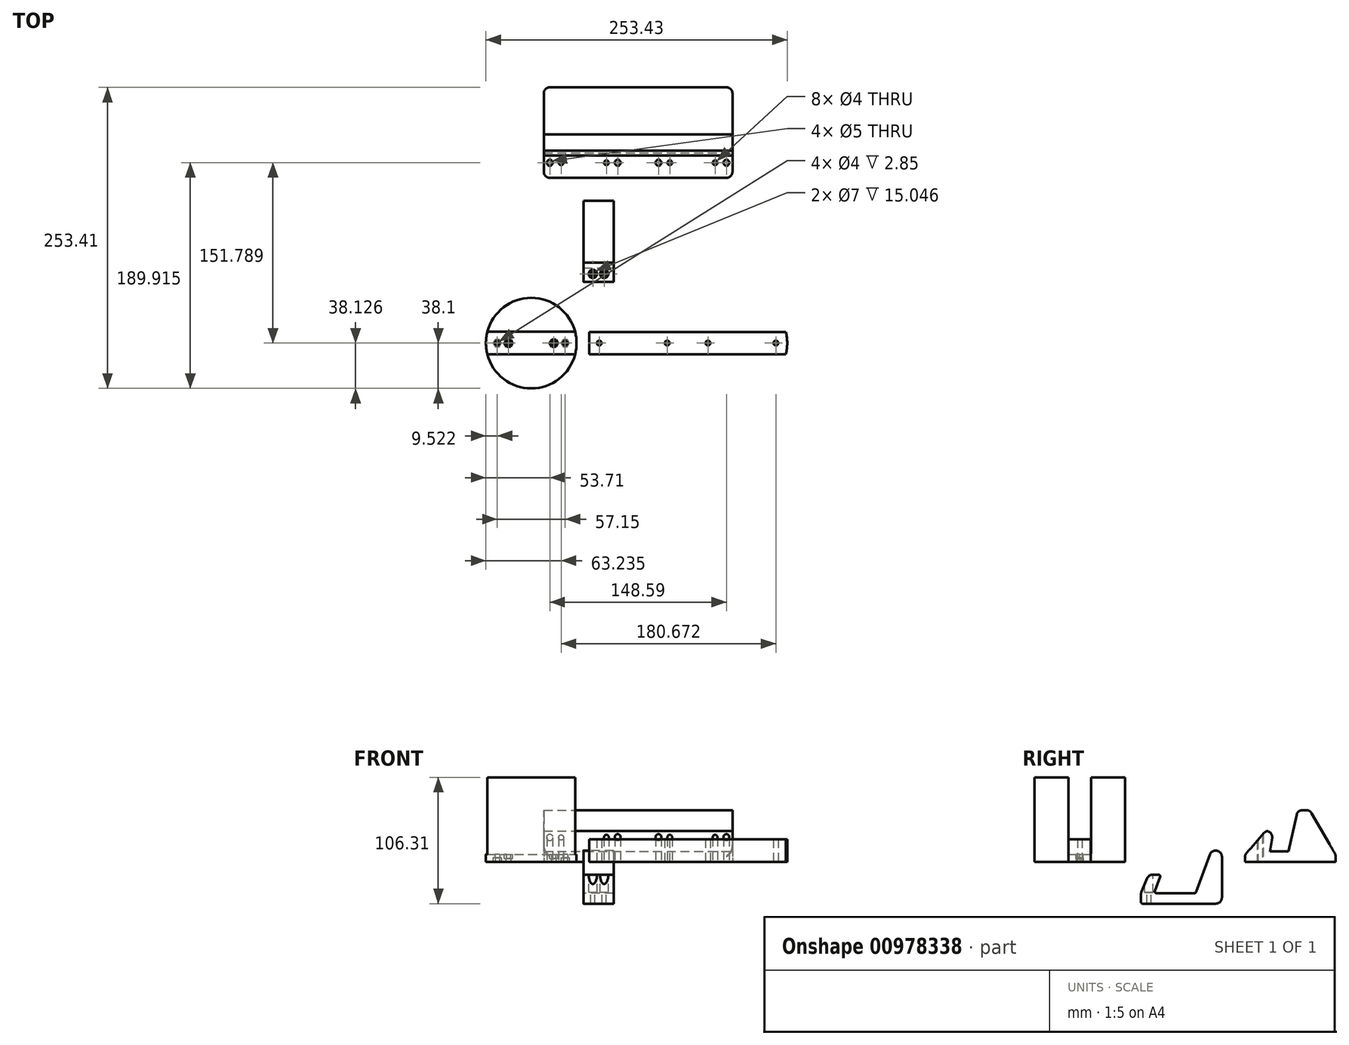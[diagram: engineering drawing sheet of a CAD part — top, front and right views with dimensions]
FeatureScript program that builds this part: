
annotation { "Feature Type Name" : "Feature", "Feature Type Description" : "" }
export const myFeature = defineFeature(function(context is Context, id is Id, definition is map)
    precondition{}
    {
        {
            var Q0;
            Q0=qCreatedBy(makeId("Top.planeOp"),FACE);
            var sketch = newSketch(context, id + "F0", { "sketchPlane" : qUnion([Q0])});
            skCircle(sketch, "E0", {"center": v(-43.87, -98.43) * mm, "radius": 38.1 * mm});
            skSolve(sketch);
        }
        {
            var Q0;
            Q0=makeQuery(id+"F0.imprint","IMPRINT",FACE,{"disambiguationData":[TD([[makeQuery(id+"F0.imprint","IMPRINT",EDGE,{"derivedFrom":sQuery(id+"F0.wireOp",EDGE,"E0")}),1.0]])]});
            extrude(context, id + "F1", {"entities" : qUnion([Q0]), "depth" : 71.12 * mm, "offsetDistance" : 25.4 * mm});
        }
        {
            var Q0;
            Q0=makeQuery(id+"F1.opExtrude","CAP_FACE",FACE,{"disambiguationData":[OSD([sQuery(id+"F0.wireOp",EDGE,"E0")])],"isStart":false});
            var sketch = newSketch(context, id + "F2", { "sketchPlane" : qUnion([Q0])});
            skCircle(sketch, "E1.0.0", {"center": v(-43.87, -98.43) * mm, "radius": 38.1 * mm, "construction": true});
            skLineSegment(sketch, "E2.bottom", {"start": v(-81.97, -88.9) * mm, "end": v(-5.77, -88.9) * mm});
            skLineSegment(sketch, "E2.top", {"start": v(-81.97, -107.96) * mm, "end": v(-5.77, -107.96) * mm});
            skLineSegment(sketch, "E2.left", {"start": v(-81.97, -88.9) * mm, "end": v(-81.97, -107.96) * mm});
            skLineSegment(sketch, "E2.right", {"start": v(-5.77, -88.9) * mm, "end": v(-5.77, -107.96) * mm});
            skSolve(sketch);
        }
        {
            var Q0;
            {var subQ0=sQuery(id+"F2.wireOp",EDGE,"E2.bottom");var subQ1=makeQuery(id+"F1.opExtrude","CAP_EDGE",EDGE,{"disambiguationData":[OSD([sQuery(id+"F0.wireOp",EDGE,"E0")])],"isStart":false});var subQ4=makeQuery(id+"F2.imprint","INTERSECT",VERTEX,{"disambiguationData":[OD(0.0)],"derivedFrom":[subQ1,subQ0]});Q0=makeQuery(id+"F2.imprint","IMPRINT",FACE,{"disambiguationData":[TD([[makeQuery(id+"F2.imprint","IMPRINT",EDGE,{"disambiguationData":[TD([[subQ4,-1.0]])],"derivedFrom":subQ0}),-1.0]])]});}
            extrude(context, id + "F3", {"entities" : qUnion([Q0]), "operationType" : NewBodyOperationType.REMOVE, "oppositeDirection" : true, "depth" : 64.77 * mm, "offsetDistance" : 25.4 * mm});
        }
        {
            var Q0;
            Q0=makeQuery(id+"F1.opExtrude","CAP_FACE",FACE,{"disambiguationData":[OSD([sQuery(id+"F0.wireOp",EDGE,"E0")])],"isStart":true});
            var sketch = newSketch(context, id + "F4", { "sketchPlane" : qUnion([Q0])});
            skArc(sketch, "E3.0.0", {"start": v(-80.76, 88.9) * mm, "mid": v(-81.97, 98.43) * mm, "end": v(-80.76, 107.96) * mm, "construction": true});
            skLineSegment(sketch, "E3.0.1", {"start": v(-80.76, 107.96) * mm, "end": v(-6.98, 107.96) * mm, "construction": true});
            skArc(sketch, "E3.0.2", {"start": v(-6.98, 107.96) * mm, "mid": v(-5.77, 98.43) * mm, "end": v(-6.98, 88.9) * mm, "construction": true});
            skLineSegment(sketch, "E3.0.3", {"start": v(-6.98, 88.9) * mm, "end": v(-80.76, 88.9) * mm, "construction": true});
            skLineSegment(sketch, "E4", {"start": v(-72.45, 98.43) * mm, "end": v(-15.3, 98.43) * mm, "construction": true});
            skCircle(sketch, "E5", {"center": v(-15.3, 98.43) * mm, "radius": 2 * mm});
            skCircle(sketch, "E6", {"center": v(-72.45, 98.43) * mm, "radius": 2 * mm});
            skCircle(sketch, "E7.cCircle", {"center": v(-72.45, 98.43) * mm, "radius": 3 * mm, "construction": true});
            skLineSegment(sketch, "E7.0", {"start": v(-74.18, 95.43) * mm, "end": v(-75.91, 98.43) * mm});
            skLineSegment(sketch, "E7.1", {"start": v(-75.91, 98.43) * mm, "end": v(-74.18, 101.43) * mm});
            skLineSegment(sketch, "E7.2", {"start": v(-74.18, 101.43) * mm, "end": v(-70.72, 101.43) * mm});
            skLineSegment(sketch, "E7.3", {"start": v(-70.72, 101.43) * mm, "end": v(-68.98, 98.43) * mm});
            skLineSegment(sketch, "E7.4", {"start": v(-68.98, 98.43) * mm, "end": v(-70.72, 95.43) * mm});
            skLineSegment(sketch, "E7.5", {"start": v(-70.72, 95.43) * mm, "end": v(-74.18, 95.43) * mm});
            skPoint(sketch, "E7.0.midPoint", {"position": v(-75.05, 96.93) * mm});
            skCircle(sketch, "E8.cCircle", {"center": v(-15.3, 98.43) * mm, "radius": 3 * mm, "construction": true});
            skLineSegment(sketch, "E8.0", {"start": v(-13.57, 95.43) * mm, "end": v(-17.03, 95.43) * mm});
            skLineSegment(sketch, "E8.1", {"start": v(-17.03, 95.43) * mm, "end": v(-18.76, 98.43) * mm});
            skLineSegment(sketch, "E8.2", {"start": v(-18.76, 98.43) * mm, "end": v(-17.03, 101.43) * mm});
            skLineSegment(sketch, "E8.3", {"start": v(-17.03, 101.43) * mm, "end": v(-13.57, 101.43) * mm});
            skLineSegment(sketch, "E8.4", {"start": v(-13.57, 101.43) * mm, "end": v(-11.83, 98.43) * mm});
            skLineSegment(sketch, "E8.5", {"start": v(-11.83, 98.43) * mm, "end": v(-13.57, 95.43) * mm});
            skPoint(sketch, "E8.0.midPoint", {"position": v(-15.3, 95.43) * mm});
            skSolve(sketch);
        }
        {
            var Q0;
            Q0=makeQuery(id+"F4.imprint","IMPRINT",FACE,{"disambiguationData":[TD([[makeQuery(id+"F4.imprint","IMPRINT",EDGE,{"derivedFrom":sQuery(id+"F4.wireOp",EDGE,"E6")}),-1.0]])]});
            var Q1;
            Q1=makeQuery(id+"F4.imprint","IMPRINT",FACE,{"disambiguationData":[TD([[makeQuery(id+"F4.imprint","IMPRINT",EDGE,{"derivedFrom":sQuery(id+"F4.wireOp",EDGE,"E5")}),-1.0]])]});
            extrude(context, id + "F5", {"entities" : qUnion([Q0, Q1]), "operationType" : NewBodyOperationType.REMOVE, "oppositeDirection" : true, "depth" : 3.5 * mm, "offsetDistance" : 25.4 * mm});
        }
        {
            var Q0;
            Q0=makeQuery(id+"F5.boolean.opBoolean","SPLIT",FACE,{"disambiguationData":[TD([makeQuery(id+"F5.opExtrude","SWEPT_FACE",FACE,{"disambiguationData":[OSD([sQuery(id+"F4.wireOp",EDGE,"E6")])]})])],"derivedFrom":makeQuery(id+"F1.opExtrude","CAP_FACE",FACE,{"disambiguationData":[OSD([sQuery(id+"F0.wireOp",EDGE,"E0")])],"isStart":true})});
            var Q1;
            Q1=makeQuery(id+"F4.imprint","IMPRINT",FACE,{"disambiguationData":[TD([[makeQuery(id+"F4.imprint","IMPRINT",EDGE,{"derivedFrom":sQuery(id+"F4.wireOp",EDGE,"E5")}),1.0]])]});
            extrude(context, id + "F6", {"entities" : qUnion([Q0, Q1]), "operationType" : NewBodyOperationType.REMOVE, "oppositeDirection" : true, "depth" : 25.4 * mm, "offsetDistance" : 25.4 * mm});
        }
        {
            var Q0;
            Q0=makeQuery(id+"F3.boolean.opBoolean","COPY",FACE,{"derivedFrom":makeQuery(id+"F3.opExtrude","CAP_FACE",FACE,{"disambiguationData":[OSD([sQuery(id+"F0.wireOp",EDGE,"E0"),sQuery(id+"F2.wireOp",EDGE,"E2.bottom"),sQuery(id+"F2.wireOp",EDGE,"E2.top")])],"isStart":false})});
            var sketch = newSketch(context, id + "F7", { "sketchPlane" : qUnion([Q0])});
            skArc(sketch, "E9.0.0", {"start": v(-80.76, -88.9) * mm, "mid": v(-81.97, -98.43) * mm, "end": v(-80.76, -107.96) * mm, "construction": true});
            skLineSegment(sketch, "E9.0.1", {"start": v(-80.76, -107.96) * mm, "end": v(-6.98, -107.96) * mm, "construction": true});
            skArc(sketch, "E9.0.2", {"start": v(-6.98, -107.96) * mm, "mid": v(-5.77, -98.43) * mm, "end": v(-6.98, -88.9) * mm, "construction": true});
            skLineSegment(sketch, "E9.0.3", {"start": v(-6.98, -88.9) * mm, "end": v(-80.76, -88.9) * mm, "construction": true});
            skCircle(sketch, "E10.0", {"center": v(-72.45, -98.43) * mm, "radius": 2 * mm, "construction": true});
            skCircle(sketch, "E11.0", {"center": v(-15.3, -98.43) * mm, "radius": 2 * mm, "construction": true});
            skLineSegment(sketch, "E12", {"start": v(-62.92, -98.43) * mm, "end": v(-24.82, -98.43) * mm, "construction": true});
            skCircle(sketch, "E13", {"center": v(-62.92, -98.43) * mm, "radius": 2 * mm});
            skCircle(sketch, "E14", {"center": v(-24.82, -98.43) * mm, "radius": 2 * mm});
            skCircle(sketch, "E15.cCircle", {"center": v(-62.92, -98.43) * mm, "radius": 3 * mm, "construction": true});
            skLineSegment(sketch, "E15.0", {"start": v(-61.2, -95.43) * mm, "end": v(-59.46, -98.43) * mm});
            skLineSegment(sketch, "E15.1", {"start": v(-59.46, -98.43) * mm, "end": v(-61.2, -101.43) * mm});
            skLineSegment(sketch, "E15.2", {"start": v(-61.2, -101.43) * mm, "end": v(-64.66, -101.43) * mm});
            skLineSegment(sketch, "E15.3", {"start": v(-64.66, -101.43) * mm, "end": v(-66.39, -98.43) * mm});
            skLineSegment(sketch, "E15.4", {"start": v(-66.39, -98.43) * mm, "end": v(-64.66, -95.43) * mm});
            skLineSegment(sketch, "E15.5", {"start": v(-64.66, -95.43) * mm, "end": v(-61.2, -95.43) * mm});
            skPoint(sketch, "E15.0.midPoint", {"position": v(-60.33, -96.93) * mm});
            skCircle(sketch, "E16.cCircle", {"center": v(-24.82, -98.43) * mm, "radius": 3 * mm, "construction": true});
            skLineSegment(sketch, "E16.0", {"start": v(-26.56, -95.43) * mm, "end": v(-23.1, -95.43) * mm});
            skLineSegment(sketch, "E16.1", {"start": v(-23.1, -95.43) * mm, "end": v(-21.36, -98.43) * mm});
            skLineSegment(sketch, "E16.2", {"start": v(-21.36, -98.43) * mm, "end": v(-23.1, -101.43) * mm});
            skLineSegment(sketch, "E16.3", {"start": v(-23.1, -101.43) * mm, "end": v(-26.56, -101.43) * mm});
            skLineSegment(sketch, "E16.4", {"start": v(-26.56, -101.43) * mm, "end": v(-28.29, -98.43) * mm});
            skLineSegment(sketch, "E16.5", {"start": v(-28.29, -98.43) * mm, "end": v(-26.56, -95.43) * mm});
            skPoint(sketch, "E16.0.midPoint", {"position": v(-24.82, -95.43) * mm});
            skSolve(sketch);
        }
        {
            var Q0;
            Q0=makeQuery(id+"F7.imprint","IMPRINT",FACE,{"disambiguationData":[TD([[makeQuery(id+"F7.imprint","IMPRINT",EDGE,{"derivedFrom":sQuery(id+"F7.wireOp",EDGE,"E13")}),-1.0]])]});
            var Q1;
            Q1=makeQuery(id+"F7.imprint","IMPRINT",FACE,{"disambiguationData":[TD([[makeQuery(id+"F7.imprint","IMPRINT",EDGE,{"derivedFrom":sQuery(id+"F7.wireOp",EDGE,"E14")}),-1.0]])]});
            extrude(context, id + "F8", {"entities" : qUnion([Q0, Q1]), "operationType" : NewBodyOperationType.REMOVE, "oppositeDirection" : true, "depth" : 3.5 * mm, "offsetDistance" : 25.4 * mm});
        }
        {
            var Q0;
            Q0=makeQuery(id+"F8.boolean.opBoolean","SPLIT",FACE,{"disambiguationData":[TD([makeQuery(id+"F8.opExtrude","SWEPT_FACE",FACE,{"disambiguationData":[OSD([sQuery(id+"F7.wireOp",EDGE,"E13")])]})])],"derivedFrom":makeQuery(id+"F3.boolean.opBoolean","COPY",FACE,{"derivedFrom":makeQuery(id+"F3.opExtrude","CAP_FACE",FACE,{"disambiguationData":[OSD([sQuery(id+"F0.wireOp",EDGE,"E0"),sQuery(id+"F2.wireOp",EDGE,"E2.bottom"),sQuery(id+"F2.wireOp",EDGE,"E2.top")])],"isStart":false})})});
            var Q1;
            Q1=makeQuery(id+"F8.boolean.opBoolean","SPLIT",FACE,{"disambiguationData":[TD([makeQuery(id+"F8.opExtrude","SWEPT_FACE",FACE,{"disambiguationData":[OSD([sQuery(id+"F7.wireOp",EDGE,"E14")])]})])],"derivedFrom":makeQuery(id+"F3.boolean.opBoolean","COPY",FACE,{"derivedFrom":makeQuery(id+"F3.opExtrude","CAP_FACE",FACE,{"disambiguationData":[OSD([sQuery(id+"F0.wireOp",EDGE,"E0"),sQuery(id+"F2.wireOp",EDGE,"E2.bottom"),sQuery(id+"F2.wireOp",EDGE,"E2.top")])],"isStart":false})})});
            extrude(context, id + "F9", {"entities" : qUnion([Q0, Q1]), "operationType" : NewBodyOperationType.REMOVE, "endBound" : BoundingType.THROUGH_ALL, "oppositeDirection" : true, "depth" : 25.4 * mm, "offsetDistance" : 25.4 * mm});
        }
        {
            var Q0;
            Q0=makeQuery(id+"F3.boolean.opBoolean","COPY",EDGE,{"derivedFrom":makeQuery(id+"F3.opExtrude","CAP_EDGE",EDGE,{"disambiguationData":[OSD([sQuery(id+"F2.wireOp",EDGE,"E2.top")])],"isStart":false})});
            var Q1;
            Q1=makeQuery(id+"F3.boolean.opBoolean","COPY",EDGE,{"derivedFrom":makeQuery(id+"F3.opExtrude","CAP_EDGE",EDGE,{"disambiguationData":[OSD([sQuery(id+"F2.wireOp",EDGE,"E2.bottom")])],"isStart":false})});
            fillet(context, id + "F10", {"entities" : qUnion([Q0, Q1]), "radius" : 0.5 * mm, "tangentPropagation" : true, "allowEdgeOverflow" : false});
        }
        {
            var Q0;
            Q0=qCreatedBy(makeId("Top.planeOp"),FACE);
            var sketch = newSketch(context, id + "F11", { "sketchPlane" : qUnion([Q0])});
            skLineSegment(sketch, "E17.bottom", {"start": v(5, -89) * mm, "end": v(170.28, -89) * mm});
            skLineSegment(sketch, "E17.top", {"start": v(5, -107.8) * mm, "end": v(170.28, -107.8) * mm});
            skLineSegment(sketch, "E17.left", {"start": v(5, -89) * mm, "end": v(5, -107.8) * mm});
            skLineSegment(sketch, "E17.right", {"start": v(170.28, -89) * mm, "end": v(170.28, -107.8) * mm, "construction": true});
            skPoint(sketch, "E17.middle", {"position": v(87.64, -98.4) * mm});
            skArc(sketch, "E18", {"start": v(5, -89) * mm, "mid": v(3.82, -98.4) * mm, "end": v(5, -107.8) * mm});
            skLineSegment(sketch, "E19", {"start": v(87.64, -89) * mm, "end": v(87.64, -107.8) * mm, "construction": true});
            skCircle(sketch, "E20", {"center": v(70.5, -98.4) * mm, "radius": 2 * mm});
            skCircle(sketch, "E21", {"center": v(13.35, -98.4) * mm, "radius": 2 * mm});
            skLineSegment(sketch, "E22", {"start": v(13.35, -98.4) * mm, "end": v(70.5, -98.4) * mm, "construction": true});
            skCircle(sketch, "E23.MirrorC", {"center": v(104.79, -98.4) * mm, "radius": 2 * mm});
            skCircle(sketch, "E24.MirrorC", {"center": v(161.94, -98.4) * mm, "radius": 2 * mm});
            skArc(sketch, "E25.MirrorCS", {"start": v(170.28, -89) * mm, "mid": v(171.46, -98.4) * mm, "end": v(170.28, -107.8) * mm});
            skCircle(sketch, "E26", {"center": v(41.92, -98.4) * mm, "radius": 38.1 * mm, "construction": true});
            skSolve(sketch);
        }
        {
            var Q0;
            Q0=makeQuery(id+"F11.imprint","IMPRINT",FACE,{"disambiguationData":[TD([[makeQuery(id+"F11.imprint","IMPRINT",EDGE,{"derivedFrom":sQuery(id+"F11.wireOp",EDGE,"E17.bottom")}),-1.0]])]});
            extrude(context, id + "F12", {"entities" : qUnion([Q0]), "depth" : 19.05 * mm, "offsetDistance" : 25.4 * mm});
        }
        {
            var Q0;
            Q0=qCreatedBy(makeId("Top.planeOp"),FACE);
            var sketch = newSketch(context, id + "F13", { "sketchPlane" : qUnion([Q0])});
            skCircle(sketch, "E27", {"center": v(-28.26, 53.38) * mm, "radius": 2.5 * mm});
            skCircle(sketch, "E28", {"center": v(-18.74, 53.38) * mm, "radius": 2 * mm});
            skCircle(sketch, "E29", {"center": v(19.36, 53.38) * mm, "radius": 2 * mm});
            skCircle(sketch, "E30", {"center": v(28.89, 53.38) * mm, "radius": 2.5 * mm});
            skLineSegment(sketch, "E31", {"start": v(-18.74, 53.38) * mm, "end": v(19.36, 53.38) * mm, "construction": true});
            skLineSegment(sketch, "E32", {"start": v(-28.26, 53.38) * mm, "end": v(-18.74, 53.38) * mm, "construction": true});
            skLineSegment(sketch, "E33", {"start": v(19.36, 53.38) * mm, "end": v(28.89, 53.38) * mm, "construction": true});
            skLineSegment(sketch, "E34", {"start": v(46.03, 60.68) * mm, "end": v(46.03, 43.66) * mm, "construction": true});
            skCircle(sketch, "E35.MirrorC", {"center": v(63.18, 53.38) * mm, "radius": 2.5 * mm});
            skCircle(sketch, "E36.MirrorC", {"center": v(72.7, 53.38) * mm, "radius": 2 * mm});
            skCircle(sketch, "E37.MirrorC", {"center": v(110.8, 53.38) * mm, "radius": 2 * mm});
            skCircle(sketch, "E38.MirrorC", {"center": v(120.33, 53.38) * mm, "radius": 2.5 * mm});
            skLineSegment(sketch, "E39.bottom", {"start": v(-33.34, 116.88) * mm, "end": v(125.4, 116.88) * mm});
            skLineSegment(sketch, "E39.top", {"start": v(-33.34, 40.68) * mm, "end": v(125.4, 40.68) * mm});
            skLineSegment(sketch, "E39.left", {"start": v(-33.34, 116.88) * mm, "end": v(-33.34, 40.68) * mm});
            skLineSegment(sketch, "E39.right", {"start": v(125.4, 116.88) * mm, "end": v(125.4, 40.68) * mm});
            skPoint(sketch, "E39.middle", {"position": v(46.03, 78.78) * mm});
            skSolve(sketch);
        }
        {
            var Q0;
            Q0=makeQuery(id+"F13.imprint","IMPRINT",FACE,{"disambiguationData":[TD([[makeQuery(id+"F13.imprint","IMPRINT",EDGE,{"derivedFrom":sQuery(id+"F13.wireOp",EDGE,"E27")}),-1.0]])]});
            extrude(context, id + "F14", {"entities" : qUnion([Q0]), "depth" : 6 * mm, "offsetDistance" : 25.4 * mm});
        }
        {
            var Q0;
            Q0=makeQuery(id+"F14.opExtrude","SWEPT_FACE",FACE,{"disambiguationData":[OSD([sQuery(id+"F13.wireOp",EDGE,"E39.right")])]});
            var sketch = newSketch(context, id + "F15", { "sketchPlane" : qUnion([Q0])});
            skLineSegment(sketch, "E40", {"start": v(40.68, 6) * mm, "end": v(58.17, 26) * mm});
            skLineSegment(sketch, "E41", {"start": v(58.17, 26) * mm, "end": v(64.4, 26) * mm});
            skLineSegment(sketch, "E42", {"start": v(64.4, 26) * mm, "end": v(61.72, 8.7) * mm});
            skLineSegment(sketch, "E43", {"start": v(61.72, 8.7) * mm, "end": v(77.3, 8.7) * mm});
            skLineSegment(sketch, "E44", {"start": v(77.3, 8.7) * mm, "end": v(84.94, 43.52) * mm});
            skLineSegment(sketch, "E45", {"start": v(84.94, 43.52) * mm, "end": v(95.26, 43.52) * mm});
            skLineSegment(sketch, "E46", {"start": v(95.26, 43.52) * mm, "end": v(116.88, 6) * mm});
            skSolve(sketch);
        }
        {
            var Q0;
            Q0=makeQuery(id+"F15.imprint","IMPRINT",FACE,{"disambiguationData":[TD([[makeQuery(id+"F15.imprint","IMPRINT",EDGE,{"derivedFrom":sQuery(id+"F15.wireOp",EDGE,"E40")}),-1.0]])]});
            var Q1;
            Q1=makeQuery(id+"F14.opExtrude","SWEPT_FACE",FACE,{"disambiguationData":[OSD([sQuery(id+"F13.wireOp",EDGE,"E39.left")])]});
            extrude(context, id + "F16", {"entities" : qUnion([Q0]), "operationType" : NewBodyOperationType.ADD, "endBound" : BoundingType.UP_TO_SURFACE, "oppositeDirection" : true, "depth" : 25.4 * mm, "endBoundEntityFace" : qUnion([Q1]), "offsetDistance" : 25.4 * mm});
        }
        {
            var Q0;
            {var subQ0=sQuery(id+"F13.wireOp",EDGE,"E39.top");Q0=makeQuery(id+"F16.boolean.opBoolean","MERGE",EDGE,{"derivedFrom":[makeQuery(id+"F14.opExtrude","CAP_EDGE",EDGE,{"disambiguationData":[OSD([subQ0])],"isStart":false}),makeQuery(id+"F16.opExtrude","SWEPT_EDGE",EDGE,{"disambiguationData":[OSD([subQ0,sQuery(id+"F13.wireOp",EDGE,"E39.right"),sQuery(id+"F15.wireOp",EDGE,"E40")])]})]});}
            var Q1;
            Q1=makeQuery(id+"F16.opExtrude","SWEPT_EDGE",EDGE,{"disambiguationData":[OSD([sQuery(id+"F15.wireOp",EDGE,"E40"),sQuery(id+"F15.wireOp",EDGE,"E41")])]});
            var Q2;
            Q2=makeQuery(id+"F14.opExtrude","SWEPT_EDGE",EDGE,{"disambiguationData":[OSD([sQuery(id+"F13.wireOp",EDGE,"E39.top"),sQuery(id+"F13.wireOp",EDGE,"E39.left")])]});
            var Q3;
            Q3=makeQuery(id+"F14.opExtrude","SWEPT_EDGE",EDGE,{"disambiguationData":[OSD([sQuery(id+"F13.wireOp",EDGE,"E39.top"),sQuery(id+"F13.wireOp",EDGE,"E39.right")])]});
            var Q4;
            {var subQ0=sQuery(id+"F13.wireOp",EDGE,"E39.bottom");Q4=makeQuery(id+"F16.boolean.opBoolean","MERGE",EDGE,{"derivedFrom":[makeQuery(id+"F14.opExtrude","CAP_EDGE",EDGE,{"disambiguationData":[OSD([subQ0])],"isStart":false}),makeQuery(id+"F16.opExtrude","SWEPT_EDGE",EDGE,{"disambiguationData":[OSD([subQ0,sQuery(id+"F13.wireOp",EDGE,"E39.right"),sQuery(id+"F15.wireOp",EDGE,"E46")])]})]});}
            var Q5;
            Q5=makeQuery(id+"F14.opExtrude","SWEPT_EDGE",EDGE,{"disambiguationData":[OSD([sQuery(id+"F13.wireOp",EDGE,"E39.bottom"),sQuery(id+"F13.wireOp",EDGE,"E39.right")])]});
            var Q6;
            Q6=makeQuery(id+"F14.opExtrude","SWEPT_EDGE",EDGE,{"disambiguationData":[OSD([sQuery(id+"F13.wireOp",EDGE,"E39.bottom"),sQuery(id+"F13.wireOp",EDGE,"E39.left")])]});
            var Q7;
            Q7=makeQuery(id+"F16.opExtrude","SWEPT_EDGE",EDGE,{"disambiguationData":[OSD([sQuery(id+"F15.wireOp",EDGE,"E45"),sQuery(id+"F15.wireOp",EDGE,"E46")])]});
            var Q8;
            Q8=makeQuery(id+"F16.opExtrude","SWEPT_EDGE",EDGE,{"disambiguationData":[OSD([sQuery(id+"F15.wireOp",EDGE,"E44"),sQuery(id+"F15.wireOp",EDGE,"E45")])]});
            var Q9;
            Q9=makeQuery(id+"F16.opExtrude","SWEPT_EDGE",EDGE,{"disambiguationData":[OSD([sQuery(id+"F15.wireOp",EDGE,"E41"),sQuery(id+"F15.wireOp",EDGE,"E42")])]});
            fillet(context, id + "F17", {"entities" : qUnion([Q0, Q1, Q2, Q3, Q4, Q5, Q6, Q7, Q8, Q9]), "radius" : 5.08 * mm, "tangentPropagation" : true, "allowEdgeOverflow" : false});
        }
        {
            var Q0;
            Q0=makeQuery(id+"F16.boolean.opBoolean","SPLIT",FACE,{"disambiguationData":[TD([makeQuery(id+"F14.opExtrude","SWEPT_FACE",FACE,{"disambiguationData":[OSD([sQuery(id+"F13.wireOp",EDGE,"E27")])]})])],"derivedFrom":makeQuery(id+"F16.opExtrude","SWEPT_FACE",FACE,{"disambiguationData":[OSD([sQuery(id+"F13.wireOp",EDGE,"E39.right")])]})});
            var Q1;
            Q1=makeQuery(id+"F16.boolean.opBoolean","SPLIT",FACE,{"disambiguationData":[TD([makeQuery(id+"F14.opExtrude","SWEPT_FACE",FACE,{"disambiguationData":[OSD([sQuery(id+"F13.wireOp",EDGE,"E28")])]})])],"derivedFrom":makeQuery(id+"F16.opExtrude","SWEPT_FACE",FACE,{"disambiguationData":[OSD([sQuery(id+"F13.wireOp",EDGE,"E39.right")])]})});
            var Q2;
            Q2=makeQuery(id+"F16.boolean.opBoolean","SPLIT",FACE,{"disambiguationData":[TD([makeQuery(id+"F14.opExtrude","SWEPT_FACE",FACE,{"disambiguationData":[OSD([sQuery(id+"F13.wireOp",EDGE,"E35.MirrorC")])]})])],"derivedFrom":makeQuery(id+"F16.opExtrude","SWEPT_FACE",FACE,{"disambiguationData":[OSD([sQuery(id+"F13.wireOp",EDGE,"E39.right")])]})});
            var Q3;
            Q3=makeQuery(id+"F16.boolean.opBoolean","SPLIT",FACE,{"disambiguationData":[TD([makeQuery(id+"F14.opExtrude","SWEPT_FACE",FACE,{"disambiguationData":[OSD([sQuery(id+"F13.wireOp",EDGE,"E30")])]})])],"derivedFrom":makeQuery(id+"F16.opExtrude","SWEPT_FACE",FACE,{"disambiguationData":[OSD([sQuery(id+"F13.wireOp",EDGE,"E39.right")])]})});
            var Q4;
            Q4=makeQuery(id+"F16.boolean.opBoolean","SPLIT",FACE,{"disambiguationData":[TD([makeQuery(id+"F14.opExtrude","SWEPT_FACE",FACE,{"disambiguationData":[OSD([sQuery(id+"F13.wireOp",EDGE,"E38.MirrorC")])]})])],"derivedFrom":makeQuery(id+"F16.opExtrude","SWEPT_FACE",FACE,{"disambiguationData":[OSD([sQuery(id+"F13.wireOp",EDGE,"E39.right")])]})});
            var Q5;
            Q5=makeQuery(id+"F16.boolean.opBoolean","SPLIT",FACE,{"disambiguationData":[TD([makeQuery(id+"F14.opExtrude","SWEPT_FACE",FACE,{"disambiguationData":[OSD([sQuery(id+"F13.wireOp",EDGE,"E37.MirrorC")])]})])],"derivedFrom":makeQuery(id+"F16.opExtrude","SWEPT_FACE",FACE,{"disambiguationData":[OSD([sQuery(id+"F13.wireOp",EDGE,"E39.right")])]})});
            var Q6;
            Q6=makeQuery(id+"F16.boolean.opBoolean","SPLIT",FACE,{"disambiguationData":[TD([makeQuery(id+"F14.opExtrude","SWEPT_FACE",FACE,{"disambiguationData":[OSD([sQuery(id+"F13.wireOp",EDGE,"E29")])]})])],"derivedFrom":makeQuery(id+"F16.opExtrude","SWEPT_FACE",FACE,{"disambiguationData":[OSD([sQuery(id+"F13.wireOp",EDGE,"E39.right")])]})});
            var Q7;
            Q7=makeQuery(id+"F16.boolean.opBoolean","SPLIT",FACE,{"disambiguationData":[TD([makeQuery(id+"F14.opExtrude","SWEPT_FACE",FACE,{"disambiguationData":[OSD([sQuery(id+"F13.wireOp",EDGE,"E36.MirrorC")])]})])],"derivedFrom":makeQuery(id+"F16.opExtrude","SWEPT_FACE",FACE,{"disambiguationData":[OSD([sQuery(id+"F13.wireOp",EDGE,"E39.right")])]})});
            extrude(context, id + "F18", {"entities" : qUnion([Q0, Q1, Q2, Q3, Q4, Q5, Q6, Q7]), "operationType" : NewBodyOperationType.REMOVE, "endBound" : BoundingType.THROUGH_ALL, "oppositeDirection" : true, "depth" : 25.4 * mm, "offsetDistance" : 25.4 * mm});
        }
        {
            var Q0;
            Q0=qCreatedBy(makeId("Right.planeOp"),FACE);
            var sketch = newSketch(context, id + "F19", { "sketchPlane" : qUnion([Q0])});
            skLineSegment(sketch, "E47", {"start": v(-46.85, -26.3) * mm, "end": v(-40.37, -10.78) * mm});
            skLineSegment(sketch, "E48", {"start": v(-40.37, -10.78) * mm, "end": v(-30.2, -10.78) * mm});
            skLineSegment(sketch, "E49", {"start": v(-30.2, -10.78) * mm, "end": v(-35.85, -26.3) * mm});
            skLineSegment(sketch, "E50", {"start": v(-35.85, -26.3) * mm, "end": v(-0.72, -26.3) * mm});
            skLineSegment(sketch, "E51", {"start": v(-0.72, -26.3) * mm, "end": v(12.32, 9.5) * mm});
            skLineSegment(sketch, "E52", {"start": v(12.32, 9.5) * mm, "end": v(21.2, 9.5) * mm});
            skLineSegment(sketch, "E53", {"start": v(21.2, 9.5) * mm, "end": v(21.2, -26.3) * mm});
            skLineSegment(sketch, "E54", {"start": v(21.2, -26.3) * mm, "end": v(21.2, -35.19) * mm});
            skLineSegment(sketch, "E55", {"start": v(21.2, -35.19) * mm, "end": v(-46.85, -35.19) * mm});
            skLineSegment(sketch, "E56", {"start": v(-46.85, -35.19) * mm, "end": v(-46.85, -26.3) * mm});
            skSolve(sketch);
        }
        {
            var Q0;
            Q0=makeQuery(id+"F19.imprint","IMPRINT",FACE,{"disambiguationData":[TD([[makeQuery(id+"F19.imprint","IMPRINT",EDGE,{"derivedFrom":sQuery(id+"F19.wireOp",EDGE,"E47")}),-1.0]])]});
            extrude(context, id + "F20", {"entities" : qUnion([Q0]), "depth" : 25.4 * mm, "offsetDistance" : 25.4 * mm});
        }
        {
            var Q0;
            Q0=makeQuery(id+"F20.opExtrude","SWEPT_EDGE",EDGE,{"disambiguationData":[OSD([sQuery(id+"F19.wireOp",EDGE,"E51"),sQuery(id+"F19.wireOp",EDGE,"E52")])]});
            var Q1;
            Q1=makeQuery(id+"F20.opExtrude","SWEPT_EDGE",EDGE,{"disambiguationData":[OSD([sQuery(id+"F19.wireOp",EDGE,"E52"),sQuery(id+"F19.wireOp",EDGE,"E53")])]});
            var Q2;
            Q2=makeQuery(id+"F20.opExtrude","SWEPT_EDGE",EDGE,{"disambiguationData":[OSD([sQuery(id+"F19.wireOp",EDGE,"E54"),sQuery(id+"F19.wireOp",EDGE,"E55")])]});
            var Q3;
            Q3=makeQuery(id+"F20.opExtrude","SWEPT_EDGE",EDGE,{"disambiguationData":[OSD([sQuery(id+"F19.wireOp",EDGE,"E47"),sQuery(id+"F19.wireOp",EDGE,"E56")])]});
            var Q4;
            Q4=makeQuery(id+"F20.opExtrude","SWEPT_EDGE",EDGE,{"disambiguationData":[OSD([sQuery(id+"F19.wireOp",EDGE,"E47"),sQuery(id+"F19.wireOp",EDGE,"E48")])]});
            fillet(context, id + "F21", {"entities" : qUnion([Q0, Q1, Q2, Q3, Q4]), "radius" : 5.08 * mm, "tangentPropagation" : true, "allowEdgeOverflow" : false});
        }
        {
            var Q0;
            Q0=makeQuery(id+"F20.opExtrude","SWEPT_EDGE",EDGE,{"disambiguationData":[OSD([sQuery(id+"F19.wireOp",EDGE,"E48"),sQuery(id+"F19.wireOp",EDGE,"E49")])]});
            var Q1;
            Q1=makeQuery(id+"F20.opExtrude","SWEPT_EDGE",EDGE,{"disambiguationData":[OSD([sQuery(id+"F19.wireOp",EDGE,"E49"),sQuery(id+"F19.wireOp",EDGE,"E50")])]});
            var Q2;
            Q2=makeQuery(id+"F20.opExtrude","SWEPT_EDGE",EDGE,{"disambiguationData":[OSD([sQuery(id+"F19.wireOp",EDGE,"E50"),sQuery(id+"F19.wireOp",EDGE,"E51")])]});
            var Q3;
            Q3=makeQuery(id+"F20.opExtrude","SWEPT_EDGE",EDGE,{"disambiguationData":[OSD([sQuery(id+"F19.wireOp",EDGE,"E55"),sQuery(id+"F19.wireOp",EDGE,"E56")])]});
            fillet(context, id + "F22", {"entities" : qUnion([Q0, Q1, Q2, Q3]), "radius" : 1.27 * mm, "tangentPropagation" : true, "allowEdgeOverflow" : false});
        }
        {
            var Q0;
            Q0=makeQuery(id+"F20.opExtrude","SWEPT_FACE",FACE,{"disambiguationData":[OSD([sQuery(id+"F19.wireOp",EDGE,"E55")])]});
            var sketch = newSketch(context, id + "F23", { "sketchPlane" : qUnion([Q0])});
            skLineSegment(sketch, "E57.0.0", {"start": v(0, 44) * mm, "end": v(0, -16.13) * mm, "construction": true});
            skLineSegment(sketch, "E57.0.1", {"start": v(0, -16.13) * mm, "end": v(25.4, -16.13) * mm, "construction": true});
            skLineSegment(sketch, "E57.0.2", {"start": v(25.4, -16.13) * mm, "end": v(25.4, 44) * mm, "construction": true});
            skLineSegment(sketch, "E57.0.3", {"start": v(25.4, 44) * mm, "end": v(0, 44) * mm, "construction": true});
            skLineSegment(sketch, "E58", {"start": v(17.46, 40.18) * mm, "end": v(55.56, 40.18) * mm, "construction": true});
            skLineSegment(sketch, "E59", {"start": v(55.56, 40.18) * mm, "end": v(65.09, 40.18) * mm, "construction": true});
            skLineSegment(sketch, "E60", {"start": v(17.46, 40.18) * mm, "end": v(7.94, 40.18) * mm, "construction": true});
            skCircle(sketch, "E61", {"center": v(7.94, 40.18) * mm, "radius": 2.5 * mm, "construction": true});
            skCircle(sketch, "E62", {"center": v(17.46, 40.18) * mm, "radius": 2 * mm, "construction": true});
            skCircle(sketch, "E63", {"center": v(55.56, 40.18) * mm, "radius": 2 * mm});
            skCircle(sketch, "E64", {"center": v(65.09, 40.18) * mm, "radius": 2.5 * mm});
            skPoint(sketch, "E65", {"position": v(12.7, 44) * mm});
            skPoint(sketch, "E66", {"position": v(36.51, 40.18) * mm});
            skPoint(sketch, "E67", {"position": v(12.7, 40.18) * mm});
            skSolve(sketch);
        }
        {
            var Q0;
            Q0=makeQuery(id+"F20.opExtrude","SWEPT_FACE",FACE,{"disambiguationData":[OSD([sQuery(id+"F19.wireOp",EDGE,"E48")])]});
            var sketch = newSketch(context, id + "F24", { "sketchPlane" : qUnion([Q0])});
            skPoint(sketch, "E68.0", {"position": v(7.94, -40.18) * mm});
            skPoint(sketch, "E69.0", {"position": v(17.46, -40.18) * mm});
            skSolve(sketch);
        }
        {
            var Q0;
            Q0=sQuery(id+"F24.wireOp",VERTEX,"E68.0");
            var Q1;
            Q1=sQuery(id+"F24.wireOp",VERTEX,"E69.0");
            var Q2;
            Q2=makeQuery(id+"F20.opExtrude","SWEPT_BODY",BODY,{"disambiguationData":[OSD([sQuery(id+"F19.wireOp",EDGE,"E47"),sQuery(id+"F19.wireOp",EDGE,"E48"),sQuery(id+"F19.wireOp",EDGE,"E49"),sQuery(id+"F19.wireOp",EDGE,"E50"),sQuery(id+"F19.wireOp",EDGE,"E51"),sQuery(id+"F19.wireOp",EDGE,"E52"),sQuery(id+"F19.wireOp",EDGE,"E53"),sQuery(id+"F19.wireOp",EDGE,"E54"),sQuery(id+"F19.wireOp",EDGE,"E55"),sQuery(id+"F19.wireOp",EDGE,"E56")])]});
            hole(context, id + "F25", {"style" : HoleStyle.C_BORE, "endStyle" : HoleEndStyle.BLIND, "holeDiameter" : 3.5 * mm, "cBoreDiameter" : 7 * mm, "cBoreDepth" : 7.11 * mm, "majorDiameter" : 6.35 * mm, "holeDepth" : 25.4 * mm, "isTappedThrough" : true, "tappedDepth" : 12.7 * mm, "tapClearance" : 3, "locations" : qUnion([Q0, Q1]), "scope" : qUnion([Q2])});
        }
    });
